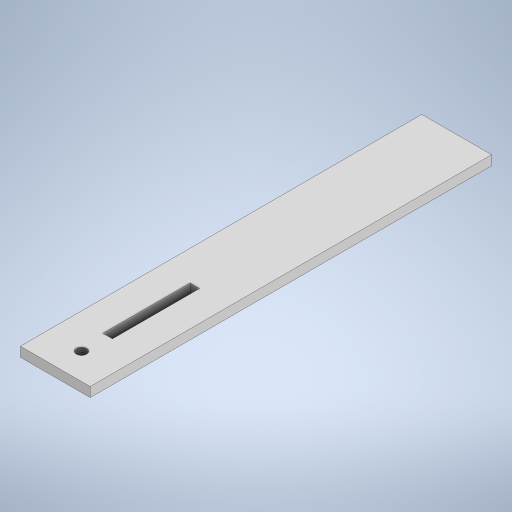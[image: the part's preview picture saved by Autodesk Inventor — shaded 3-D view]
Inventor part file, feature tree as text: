
AUTODESK INVENTOR PART (.ipt)
format: ipt  version: 2023 (Build 270158000, 158)  size: 242,176 bytes
history: native  units: mm
features: sketch x3, extrude x2, hole x1
ambient origin geometry x8: Origin, YZ Plane, XZ Plane, XY Plane, X Axis, Y Axis, Z Axis, Center Point
bodies: Solid1 (feature_tree)
feature tree (6):
  extrude  "Extrusion1"  Depth=40.0mm
  extrude  "Extrusion2"  Depth=30.0mm
  hole  "Hole1"  [1 undecoded]
  sketch  "Sketch1"  dims[d0=230.0mm d1=40.0mm]
  sketch  "Sketch2"  dims[d2=5.5mm d3=0.0mm d4=30.0mm]
  sketch  "Sketch3"  dims[d5=2.75mm d6=50.0mm d7=5.5mm d8=0.0mm d9=15.0mm d10=5.917468mm d11=14.0mm d12=4.0mm d13=2.0mm d14=90.0deg d15=19.1mm d16=20.594885mm]
note: 1 required parameter value undecoded (feature->parameter linkage not recoverable at this tier; creation-order binding heuristic only, values carry confidence <= 0.55)
